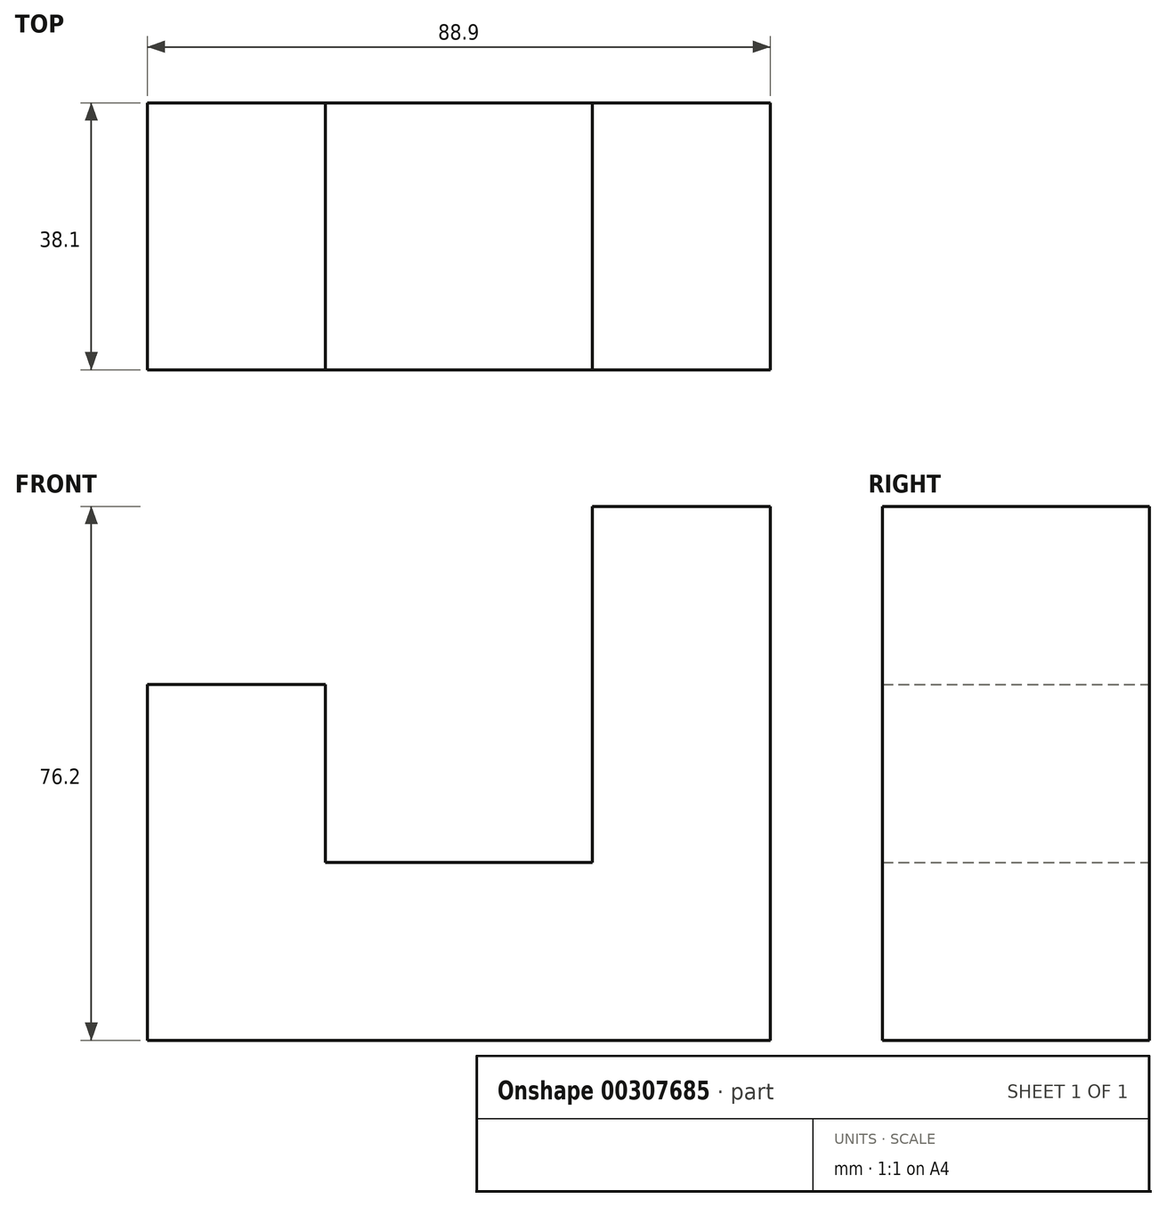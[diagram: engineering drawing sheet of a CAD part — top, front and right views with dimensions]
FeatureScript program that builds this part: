
annotation { "Feature Type Name" : "Feature", "Feature Type Description" : "" }
export const myFeature = defineFeature(function(context is Context, id is Id, definition is map)
    precondition{}
    {
        {
            var Q0;
            Q0=qCreatedBy(makeId("Front.planeOp"),FACE);
            var sketch = newSketch(context, id + "F0", { "sketchPlane" : qUnion([Q0])});
            skLineSegment(sketch, "E0", {"start": v(-43.01, -37.36) * mm, "end": v(45.89, -37.36) * mm});
            skLineSegment(sketch, "E1", {"start": v(45.89, -37.36) * mm, "end": v(45.89, 38.84) * mm});
            skLineSegment(sketch, "E2", {"start": v(45.89, 38.84) * mm, "end": v(20.49, 38.84) * mm});
            skLineSegment(sketch, "E3", {"start": v(20.49, 38.84) * mm, "end": v(20.49, -11.96) * mm});
            skLineSegment(sketch, "E4", {"start": v(20.49, -11.96) * mm, "end": v(-17.61, -11.96) * mm});
            skLineSegment(sketch, "E5", {"start": v(-17.61, -11.96) * mm, "end": v(-17.61, 13.44) * mm});
            skLineSegment(sketch, "E6", {"start": v(-17.61, 13.44) * mm, "end": v(-43.01, 13.44) * mm});
            skLineSegment(sketch, "E7", {"start": v(-43.01, 13.44) * mm, "end": v(-43.01, -37.36) * mm});
            skSolve(sketch);
        }
        {
            var Q0;
            Q0=makeQuery(id+"F0.imprint","IMPRINT",FACE,{"disambiguationData":[TD([[makeQuery(id+"F0.imprint","IMPRINT",EDGE,{"derivedFrom":sQuery(id+"F0.wireOp",EDGE,"E0")}),1.0]])]});
            extrude(context, id + "F1", {"entities" : qUnion([Q0]), "depth" : 38.1 * mm});
        }
    });
